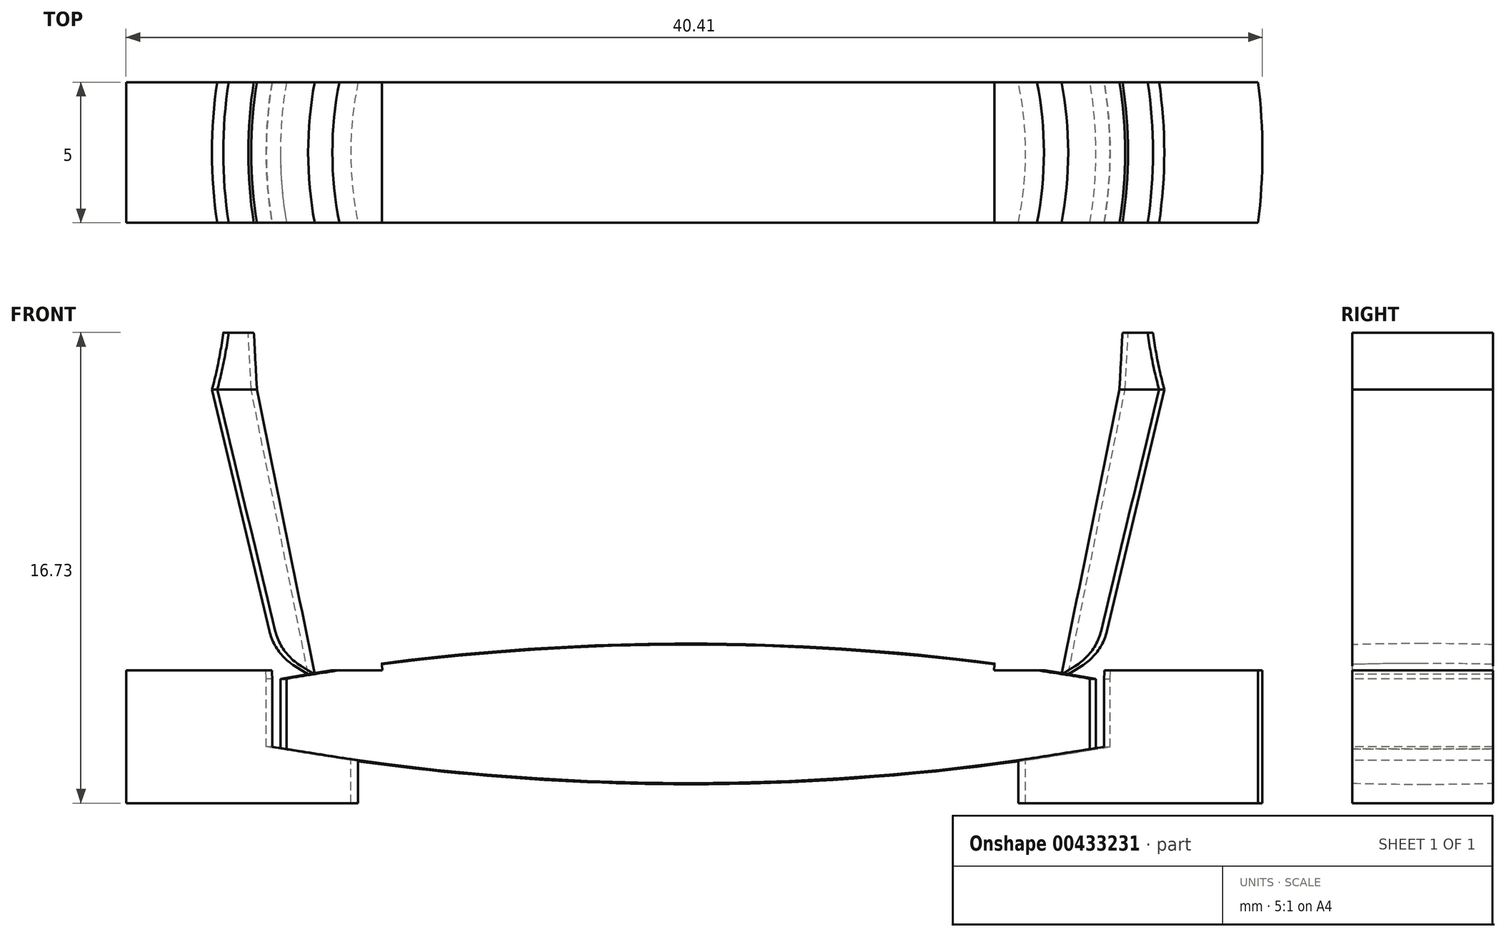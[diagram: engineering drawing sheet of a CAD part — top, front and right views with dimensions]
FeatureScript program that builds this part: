
annotation { "Feature Type Name" : "Feature", "Feature Type Description" : "" }
export const myFeature = defineFeature(function(context is Context, id is Id, definition is map)
    precondition{}
    {
        {
            var Q0;
            Q0=qCreatedBy(makeId("Front.planeOp"),FACE);
            var sketch = newSketch(context, id + "F0", { "sketchPlane" : qUnion([Q0])});
            skArc(sketch, "E0", {"start": v(0, 2.5) * mm, "mid": v(-7.28, 2.19) * mm, "end": v(-14.5, 1.25) * mm});
            skLineSegment(sketch, "E1", {"start": v(-14.5, 1.25) * mm, "end": v(-14.5, 0) * mm});
            skLineSegment(sketch, "E2.MirrorCS", {"start": v(-14.5, -1.25) * mm, "end": v(-14.5, 0) * mm});
            skArc(sketch, "E3.MirrorCS", {"start": v(0, -2.5) * mm, "mid": v(-7.28, -2.19) * mm, "end": v(-14.5, -1.25) * mm});
            skArc(sketch, "E4.MirrorCS", {"start": v(0, 2.5) * mm, "mid": v(7.28, 2.19) * mm, "end": v(14.5, 1.25) * mm, "construction": true});
            skLineSegment(sketch, "E5.MirrorCS", {"start": v(14.5, 1.25) * mm, "end": v(14.5, 0) * mm, "construction": true});
            skLineSegment(sketch, "E6.MirrorCS", {"start": v(14.5, -1.25) * mm, "end": v(14.5, 0) * mm, "construction": true});
            skArc(sketch, "E7.MirrorCS", {"start": v(0, -2.5) * mm, "mid": v(7.28, -2.19) * mm, "end": v(14.5, -1.25) * mm, "construction": true});
            skLineSegment(sketch, "E8", {"start": v(0, 2.5) * mm, "end": v(0, -2.5) * mm});
            skSolve(sketch);
        }
        {
            var Q0;
            Q0=makeQuery(id+"F0.imprint","IMPRINT",FACE,{"disambiguationData":[TD([[makeQuery(id+"F0.imprint","IMPRINT",EDGE,{"derivedFrom":sQuery(id+"F0.wireOp",EDGE,"E0")}),1.0]])]});
            var Q1;
            Q1=sQuery(id+"F0.wireOp",EDGE,"E8");
            revolve(context, id + "F1", {"entities" : qUnion([Q0]), "axis" : qUnion([Q1]), "revolveType" : RevolveType.FULL});
        }
        {
            var Q0;
            Q0=qCreatedBy(makeId("Front.planeOp"),FACE);
            var sketch = newSketch(context, id + "F2", { "sketchPlane" : qUnion([Q0])});
            skLineSegment(sketch, "E9", {"start": v(-15, 1.25) * mm, "end": v(-15, -1.17) * mm});
            skLineSegment(sketch, "E10", {"start": v(-15, -1.17) * mm, "end": v(-12, -1.65) * mm});
            skLineSegment(sketch, "E11", {"start": v(-12, -1.65) * mm, "end": v(-12, -4.65) * mm});
            skLineSegment(sketch, "E12", {"start": v(-12, -4.65) * mm, "end": v(-20.42, -4.65) * mm});
            skLineSegment(sketch, "E13", {"start": v(-20.42, -4.65) * mm, "end": v(-20.42, 5.35) * mm});
            skLineSegment(sketch, "E14", {"start": v(-20.42, 25.35) * mm, "end": v(-20.42, 28.35) * mm});
            skLineSegment(sketch, "E15", {"start": v(-20.42, 28.35) * mm, "end": v(-16.42, 28.35) * mm});
            skArc(sketch, "E16", {"start": v(-20.42, 5.35) * mm, "mid": v(-16.42, 15.35) * mm, "end": v(-20.42, 25.35) * mm});
            skLineSegment(sketch, "E17", {"start": v(-20.42, 25.35) * mm, "end": v(-16.42, 25.35) * mm, "construction": true});
            skPoint(sketch, "E17.endSnap0", {"position": v(-16.42, 15.35) * mm});
            skLineSegment(sketch, "E18", {"start": v(-16.42, 25.35) * mm, "end": v(-16.42, 5.35) * mm, "construction": true});
            skLineSegment(sketch, "E19", {"start": v(-16.42, 5.35) * mm, "end": v(-20.42, 5.35) * mm, "construction": true});
            skLineSegment(sketch, "E20", {"start": v(-15, 1.25) * mm, "end": v(-16.42, 28.35) * mm});
            skSolve(sketch);
        }
        {
            var Q0;
            Q0=makeQuery(id+"F2.imprint","IMPRINT",FACE,{"disambiguationData":[TD([[makeQuery(id+"F2.imprint","IMPRINT",EDGE,{"derivedFrom":sQuery(id+"F2.wireOp",EDGE,"E9")}),-1.0]])]});
            var Q1;
            Q1=sQuery(id+"F0.wireOp",EDGE,"E8");
            revolve(context, id + "F3", {"entities" : qUnion([Q0]), "axis" : qUnion([Q1]), "revolveType" : RevolveType.FULL});
        }
        {
            var Q0;
            Q0=qCreatedBy(makeId("Front.planeOp"),FACE);
            var sketch = newSketch(context, id + "F4", { "sketchPlane" : qUnion([Q0])});
            skLineSegment(sketch, "E21", {"start": v(-10.88, 1.55) * mm, "end": v(-11.4, 11.54) * mm});
            skLineSegment(sketch, "E22", {"start": v(-11.4, 11.54) * mm, "end": v(-29.76, 11.54) * mm});
            skLineSegment(sketch, "E23", {"start": v(-29.76, 11.54) * mm, "end": v(-29.76, 1.55) * mm});
            skLineSegment(sketch, "E24", {"start": v(-29.76, 1.55) * mm, "end": v(-10.88, 1.55) * mm});
            skLineSegment(sketch, "E25.MirrorCS", {"start": v(11.4, 11.54) * mm, "end": v(29.76, 11.54) * mm});
            skLineSegment(sketch, "E26.MirrorCS", {"start": v(10.88, 1.55) * mm, "end": v(11.4, 11.54) * mm});
            skLineSegment(sketch, "E27.MirrorCS", {"start": v(29.76, 11.54) * mm, "end": v(29.76, 1.55) * mm});
            skLineSegment(sketch, "E28.MirrorCS", {"start": v(29.76, 1.55) * mm, "end": v(10.88, 1.55) * mm});
            skSolve(sketch);
        }
        {
            var Q0;
            Q0 = qSketchRegion(id + "F4", true);
            extrude(context, id + "F5", {"entities" : qUnion([Q0]), "operationType" : NewBodyOperationType.REMOVE, "endBound" : BoundingType.SYMMETRIC, "oppositeDirection" : true, "depth" : 7 * mm});
        }
        {
            var Q0;
            Q0=qCreatedBy(makeId("Front.planeOp"),FACE);
            var sketch = newSketch(context, id + "F6", { "sketchPlane" : qUnion([Q0])});
            skLineSegment(sketch, "E29", {"start": v(-15.54, 11.54) * mm, "end": v(-16.93, 11.54) * mm});
            skLineSegment(sketch, "E30", {"start": v(-16.93, 11.54) * mm, "end": v(-14.7, 2.14) * mm});
            skLineSegment(sketch, "E31", {"start": v(-14.7, 2.14) * mm, "end": v(-13.51, 1.42) * mm});
            skLineSegment(sketch, "E32", {"start": v(-13.51, 1.42) * mm, "end": v(-15.54, 11.54) * mm});
            skSolve(sketch);
        }
        {
            var Q0;
            Q0 = qSketchRegion(id + "F6", true);
            var Q1;
            Q1=sQuery(id+"F0.wireOp",EDGE,"E8");
            revolve(context, id + "F7", {"entities" : qUnion([Q0]), "axis" : qUnion([Q1]), "revolveType" : RevolveType.FULL});
        }
        {
            var Q0;
            Q0=qCreatedBy(makeId("Front.planeOp"),FACE);
            var sketch = newSketch(context, id + "F8", { "sketchPlane" : qUnion([Q0])});
            skLineSegment(sketch, "E33.bottom", {"start": v(-19.99, 13.56) * mm, "end": v(22.86, 13.56) * mm});
            skLineSegment(sketch, "E33.top", {"start": v(-19.99, -3.17) * mm, "end": v(22.86, -3.17) * mm});
            skLineSegment(sketch, "E33.left", {"start": v(-19.99, 13.56) * mm, "end": v(-19.99, -3.17) * mm});
            skLineSegment(sketch, "E33.right", {"start": v(22.86, 13.56) * mm, "end": v(22.86, -3.17) * mm});
            skSolve(sketch);
        }
        {
            var Q0;
            Q0 = qSketchRegion(id + "F8", true);
            extrude(context, id + "F9", {"entities" : qUnion([Q0]), "operationType" : NewBodyOperationType.INTERSECT, "endBound" : BoundingType.SYMMETRIC, "oppositeDirection" : true, "depth" : 5 * mm});
        }
        {
            var Q0;
            Q0=makeQuery(id+"F3.opRevolve","SWEPT_EDGE",EDGE,{"disambiguationData":[OSD([sQuery(id+"F2.wireOp",EDGE,"E13"),sQuery(id+"F2.wireOp",EDGE,"E16")])]});
            var Q1;
            Q1=makeQuery(id+"F3.opRevolve","SWEPT_EDGE",EDGE,{"disambiguationData":[OSD([sQuery(id+"F2.wireOp",EDGE,"E14"),sQuery(id+"F2.wireOp",EDGE,"E16")])]});
            var Q2;
            Q2=makeQuery(id+"F3.opRevolve","SWEPT_EDGE",EDGE,{"disambiguationData":[OSD([sQuery(id+"F2.wireOp",EDGE,"E14"),sQuery(id+"F2.wireOp",EDGE,"E15")])]});
            var Q3;
            Q3=makeQuery(id+"F9.boolean.opBoolean","INTERSECT",EDGE,{"disambiguationData":[OD(0.0)],"derivedFrom":[makeQuery(id+"F7.opRevolve","SWEPT_FACE",FACE,{"disambiguationData":[OSD([sQuery(id+"F6.wireOp",EDGE,"E29")])]}),makeQuery(id+"F9.boolean.toolComplement.opBoolean","COPY",FACE,{"derivedFrom":makeQuery(id+"F9.opExtrude","CAP_FACE",FACE,{"disambiguationData":[OSD([sQuery(id+"F8.wireOp",EDGE,"E33.bottom"),sQuery(id+"F8.wireOp",EDGE,"E33.top"),sQuery(id+"F8.wireOp",EDGE,"E33.left"),sQuery(id+"F8.wireOp",EDGE,"E33.right")])],"isStart":false})})]});
            var Q4;
            Q4=makeQuery(id+"F9.boolean.opBoolean","INTERSECT",EDGE,{"disambiguationData":[OD(0.0)],"derivedFrom":[makeQuery(id+"F7.opRevolve","SWEPT_FACE",FACE,{"disambiguationData":[OSD([sQuery(id+"F6.wireOp",EDGE,"E29")])]}),makeQuery(id+"F9.boolean.toolComplement.opBoolean","COPY",FACE,{"derivedFrom":makeQuery(id+"F9.opExtrude","CAP_FACE",FACE,{"disambiguationData":[OSD([sQuery(id+"F8.wireOp",EDGE,"E33.bottom"),sQuery(id+"F8.wireOp",EDGE,"E33.top"),sQuery(id+"F8.wireOp",EDGE,"E33.left"),sQuery(id+"F8.wireOp",EDGE,"E33.right")])],"isStart":true})})]});
            var Q5;
            Q5=makeQuery(id+"F9.boolean.opBoolean","INTERSECT",EDGE,{"disambiguationData":[OD(1.0)],"derivedFrom":[makeQuery(id+"F7.opRevolve","SWEPT_FACE",FACE,{"disambiguationData":[OSD([sQuery(id+"F6.wireOp",EDGE,"E29")])]}),makeQuery(id+"F9.boolean.toolComplement.opBoolean","COPY",FACE,{"derivedFrom":makeQuery(id+"F9.opExtrude","CAP_FACE",FACE,{"disambiguationData":[OSD([sQuery(id+"F8.wireOp",EDGE,"E33.bottom"),sQuery(id+"F8.wireOp",EDGE,"E33.top"),sQuery(id+"F8.wireOp",EDGE,"E33.left"),sQuery(id+"F8.wireOp",EDGE,"E33.right")])],"isStart":false})})]});
            var Q6;
            Q6=makeQuery(id+"F9.boolean.opBoolean","INTERSECT",EDGE,{"disambiguationData":[OD(1.0)],"derivedFrom":[makeQuery(id+"F7.opRevolve","SWEPT_FACE",FACE,{"disambiguationData":[OSD([sQuery(id+"F6.wireOp",EDGE,"E29")])]}),makeQuery(id+"F9.boolean.toolComplement.opBoolean","COPY",FACE,{"derivedFrom":makeQuery(id+"F9.opExtrude","CAP_FACE",FACE,{"disambiguationData":[OSD([sQuery(id+"F8.wireOp",EDGE,"E33.bottom"),sQuery(id+"F8.wireOp",EDGE,"E33.top"),sQuery(id+"F8.wireOp",EDGE,"E33.left"),sQuery(id+"F8.wireOp",EDGE,"E33.right")])],"isStart":true})})]});
            var Q7;
            Q7=makeQuery(id+"F9.boolean.opBoolean","SPLIT",EDGE,{"disambiguationData":[OD(1.0)],"derivedFrom":makeQuery(id+"F7.opRevolve","SWEPT_EDGE",EDGE,{"disambiguationData":[OSD([sQuery(id+"F6.wireOp",EDGE,"E30"),sQuery(id+"F6.wireOp",EDGE,"E31")])]})});
            var Q8;
            Q8=makeQuery(id+"F9.boolean.opBoolean","SPLIT",EDGE,{"disambiguationData":[OD(0.0)],"derivedFrom":makeQuery(id+"F7.opRevolve","SWEPT_EDGE",EDGE,{"disambiguationData":[OSD([sQuery(id+"F6.wireOp",EDGE,"E30"),sQuery(id+"F6.wireOp",EDGE,"E31")])]})});
            var Q9;
            Q9=makeQuery(id+"F3.opRevolve","SWEPT_EDGE",EDGE,{"disambiguationData":[OSD([sQuery(id+"F2.wireOp",EDGE,"E12"),sQuery(id+"F2.wireOp",EDGE,"E13")])]});
            fillet(context, id + "F10", {"entities" : qUnion([Q0, Q1, Q2, Q3, Q4, Q5, Q6, Q7, Q8, Q9]), "radius" : 2 * mm, "tangentPropagation" : true, "allowEdgeOverflow" : false});
        }
    });
